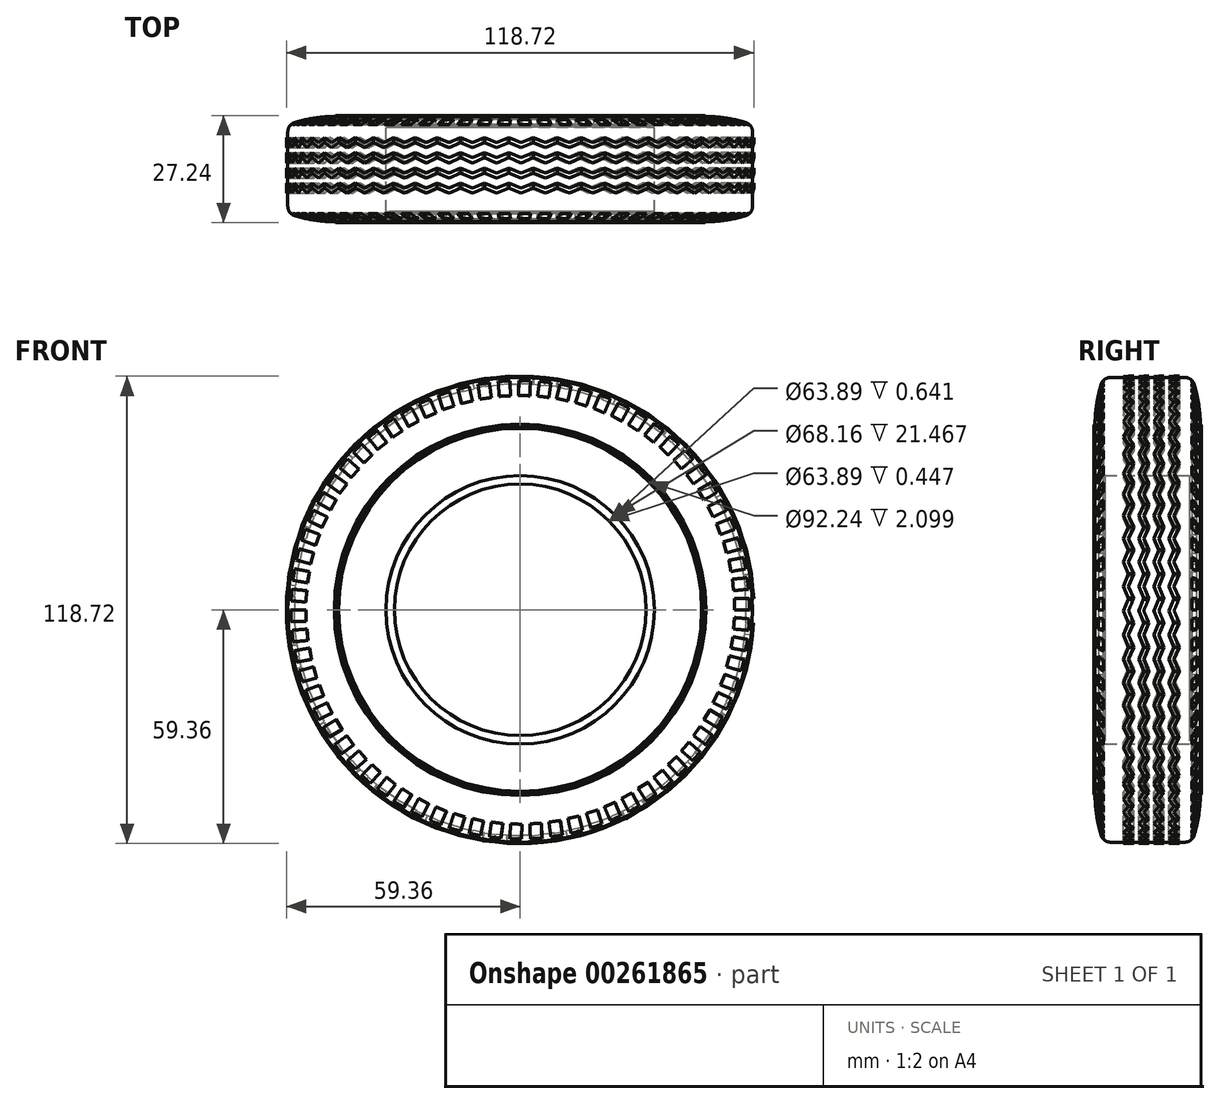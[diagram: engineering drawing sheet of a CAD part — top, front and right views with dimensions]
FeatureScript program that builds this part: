
annotation { "Feature Type Name" : "Feature", "Feature Type Description" : "" }
export const myFeature = defineFeature(function(context is Context, id is Id, definition is map)
    precondition{}
    {
        {
            var Q0;
            Q0=qCreatedBy(makeId("Front.planeOp"),FACE);
            var sketch = newSketch(context, id + "F0", { "sketchPlane" : qUnion([Q0])});
            skCircle(sketch, "E0", {"center": v(0, 0) * mm, "radius": 33.8 * mm});
            skSolve(sketch);
        }
        {
            var Q0;
            Q0=qCreatedBy(makeId("Top.planeOp"),FACE);
            var sketch = newSketch(context, id + "F1", { "sketchPlane" : qUnion([Q0])});
            skLineSegment(sketch, "E1", {"start": v(31.95, 0) * mm, "end": v(34.08, 0) * mm});
            skLineSegment(sketch, "E2", {"start": v(34.08, 22.56) * mm, "end": v(31.95, 22.56) * mm});
            skLineSegment(sketch, "E3", {"start": v(31.95, 22.56) * mm, "end": v(31.95, 21.91) * mm});
            skLineSegment(sketch, "E4", {"start": v(31.95, 21.91) * mm, "end": v(34.08, 21.91) * mm});
            skLineSegment(sketch, "E5", {"start": v(31.95, 0) * mm, "end": v(31.95, 0.45) * mm});
            skLineSegment(sketch, "E6", {"start": v(31.95, 0.45) * mm, "end": v(34.08, 0.45) * mm});
            skArc(sketch, "E7", {"start": v(59.04, 22.56) * mm, "mid": v(53.2, 24.07) * mm, "end": v(47.2, 24.65) * mm});
            skArc(sketch, "E8", {"start": v(34.08, 0) * mm, "mid": v(40.02, -1.54) * mm, "end": v(46.12, -2.1) * mm});
            skLineSegment(sketch, "E9", {"start": v(34.08, 21.91) * mm, "end": v(34.08, 0.45) * mm});
            skLineSegment(sketch, "E10", {"start": v(59.04, 22.56) * mm, "end": v(59.04, 0) * mm});
            skLineSegment(sketch, "E11", {"start": v(59.04, 22.56) * mm, "end": v(54.42, 22.56) * mm});
            skLineSegment(sketch, "E12", {"start": v(54.42, 22.56) * mm, "end": v(54.42, 23.84) * mm});
            skLineSegment(sketch, "E13", {"start": v(54.42, -1.28) * mm, "end": v(54.42, 0) * mm});
            skLineSegment(sketch, "E14", {"start": v(54.42, 0) * mm, "end": v(59.04, 0) * mm});
            skLineSegment(sketch, "E15", {"start": v(47.2, 24.65) * mm, "end": v(46.92, 24.9) * mm});
            skLineSegment(sketch, "E16", {"start": v(47.2, -2.1) * mm, "end": v(46.91, -2.34) * mm});
            skLineSegment(sketch, "E17", {"start": v(46.92, 24.9) * mm, "end": v(46.4, 24.9) * mm});
            skLineSegment(sketch, "E18", {"start": v(46.4, 24.9) * mm, "end": v(46.12, 24.65) * mm});
            skLineSegment(sketch, "E19", {"start": v(46.91, -2.34) * mm, "end": v(46.41, -2.34) * mm});
            skLineSegment(sketch, "E20", {"start": v(46.41, -2.34) * mm, "end": v(46.12, -2.1) * mm});
            skLineSegment(sketch, "E21", {"start": v(46.12, -2.1) * mm, "end": v(46.12, -2.1) * mm});
            skArc(sketch, "E22", {"start": v(47.2, -2.1) * mm, "mid": v(53.2, -1.52) * mm, "end": v(59.04, 0) * mm});
            skArc(sketch, "E23", {"start": v(46.12, 24.65) * mm, "mid": v(40.02, 24.1) * mm, "end": v(34.08, 22.56) * mm});
            skLineSegment(sketch, "E24", {"start": v(34.08, 0) * mm, "end": v(46.12, 0) * mm});
            skLineSegment(sketch, "E25", {"start": v(46.12, 0) * mm, "end": v(46.12, -2.1) * mm});
            skLineSegment(sketch, "E26", {"start": v(34.08, 22.56) * mm, "end": v(46.12, 22.56) * mm});
            skLineSegment(sketch, "E27", {"start": v(46.12, 22.56) * mm, "end": v(46.12, 24.65) * mm});
            skSolve(sketch);
        }
        {
            var Q0;
            Q0=makeQuery(id+"F1.imprint","IMPRINT",FACE,{"disambiguationData":[TD([[makeQuery(id+"F1.imprint","IMPRINT",EDGE,{"derivedFrom":sQuery(id+"F1.wireOp",EDGE,"E1")}),1.0]])]});
            var Q1;
            {var subQ0=sQuery(id+"F1.wireOp",EDGE,"E11");Q1=makeQuery(id+"F1.imprint","IMPRINT",FACE,{"disambiguationData":[TD([[makeQuery(id+"F1.imprint","IMPRINT",EDGE,{"derivedFrom":subQ0}),-1.0]])]});}
            var Q2;
            {var subQ2=sQuery(id+"F1.wireOp",EDGE,"E13");Q2=makeQuery(id+"F1.imprint","IMPRINT",FACE,{"disambiguationData":[TD([[makeQuery(id+"F1.imprint","IMPRINT",EDGE,{"derivedFrom":subQ2}),-1.0]])]});}
            var Q3;
            Q3=sQuery(id+"F0.wireOp",EDGE,"E0");
            revolve(context, id + "F2", {"entities" : qUnion([Q0, Q1, Q2]), "axis" : qUnion([Q3]), "revolveType" : RevolveType.FULL});
        }
        {
            var Q0;
            {var subQ0=sQuery(id+"F1.wireOp",EDGE,"E10");var subQ1=sQuery(id+"F1.wireOp",EDGE,"E14");Q0=makeQuery(id+"F6.opBoolean","SPLIT",EDGE,{"disambiguationData":[topologyDisambiguationEdgeConnected([makeQuery(id+"F2.opRevolve","SWEPT_FACE",FACE,{"disambiguationData":[OSD([subQ0])]}),makeQuery(id+"F5.opPattern","COPY",FACE,{"derivedFrom":makeQuery(id+"F4.opExtrude","SWEPT_FACE",FACE,{"disambiguationData":[OSD([subQ1])]}),"instanceName":"15"})])],"derivedFrom":makeQuery(id+"F2.opRevolve","SWEPT_EDGE",EDGE,{"disambiguationData":[OSD([subQ0,subQ1,sQuery(id+"F1.wireOp",EDGE,"E22")])]})});}
            var Q1;
            Q1=makeQuery(id+"F2.opRevolve","SWEPT_EDGE",EDGE,{"disambiguationData":[OSD([sQuery(id+"F1.wireOp",EDGE,"E7"),sQuery(id+"F1.wireOp",EDGE,"E10"),sQuery(id+"F1.wireOp",EDGE,"E11")])]});
            fillet(context, id + "F3", {"entities" : qUnion([Q0, Q1]), "radius" : 2.54 * mm, "tangentPropagation" : true, "allowEdgeOverflow" : false});
        }
        {
            var Q0;
            {var subQ0=sQuery(id+"F1.wireOp",EDGE,"E11");Q0=makeQuery(id+"F1.imprint","IMPRINT",FACE,{"disambiguationData":[TD([[makeQuery(id+"F1.imprint","IMPRINT",EDGE,{"derivedFrom":subQ0}),-1.0]])]});}
            var Q1;
            {var subQ2=sQuery(id+"F1.wireOp",EDGE,"E13");Q1=makeQuery(id+"F1.imprint","IMPRINT",FACE,{"disambiguationData":[TD([[makeQuery(id+"F1.imprint","IMPRINT",EDGE,{"derivedFrom":subQ2}),-1.0]])]});}
            extrude(context, id + "F4", {"entities" : qUnion([Q0, Q1]), "depth" : 2.92 * mm});
        }
        {
            var Q0;
            Q0=makeQuery(id+"F4.opExtrude","SWEPT_BODY",BODY,{"disambiguationData":[OSD([sQuery(id+"F1.wireOp",EDGE,"E7"),sQuery(id+"F1.wireOp",EDGE,"E11"),sQuery(id+"F1.wireOp",EDGE,"E12")])]});
            var Q1;
            Q1=makeQuery(id+"F4.opExtrude","SWEPT_BODY",BODY,{"disambiguationData":[OSD([sQuery(id+"F1.wireOp",EDGE,"E8"),sQuery(id+"F1.wireOp",EDGE,"E13"),sQuery(id+"F1.wireOp",EDGE,"E14")])]});
            var Q2;
            Q2=makeQuery(id+"F2.opRevolve","SWEPT_EDGE",EDGE,{"disambiguationData":[OSD([sQuery(id+"F1.wireOp",EDGE,"E1"),sQuery(id+"F1.wireOp",EDGE,"E5")])]});
            circularPattern(context, id + "F5", {"entities" : qUnion([Q0, Q1]), "axis" : qUnion([Q2]), "angle" : 360 * degree, "instanceCount" : 70, "equalSpace" : true});
        }
        {
            var Q0;
            Q0=makeQuery(id+"F4.opExtrude","SWEPT_BODY",BODY,{"disambiguationData":[OSD([sQuery(id+"F1.wireOp",EDGE,"E7"),sQuery(id+"F1.wireOp",EDGE,"E11"),sQuery(id+"F1.wireOp",EDGE,"E12")])]});
            var Q1;
            Q1=makeQuery(id+"F4.opExtrude","SWEPT_BODY",BODY,{"disambiguationData":[OSD([sQuery(id+"F1.wireOp",EDGE,"E8"),sQuery(id+"F1.wireOp",EDGE,"E13"),sQuery(id+"F1.wireOp",EDGE,"E14")])]});
            var Q2;
            Q2=makeQuery(id+"F5.opPattern","COPY",BODY,{"derivedFrom":makeQuery(id+"F4.opExtrude","SWEPT_BODY",BODY,{"disambiguationData":[OSD([sQuery(id+"F1.wireOp",EDGE,"E7"),sQuery(id+"F1.wireOp",EDGE,"E11"),sQuery(id+"F1.wireOp",EDGE,"E12")])]}),"instanceName":"1"});
            var Q3;
            Q3=makeQuery(id+"F5.opPattern","COPY",BODY,{"derivedFrom":makeQuery(id+"F4.opExtrude","SWEPT_BODY",BODY,{"disambiguationData":[OSD([sQuery(id+"F1.wireOp",EDGE,"E8"),sQuery(id+"F1.wireOp",EDGE,"E13"),sQuery(id+"F1.wireOp",EDGE,"E14")])]}),"instanceName":"1"});
            var Q4;
            Q4=makeQuery(id+"F5.opPattern","COPY",BODY,{"derivedFrom":makeQuery(id+"F4.opExtrude","SWEPT_BODY",BODY,{"disambiguationData":[OSD([sQuery(id+"F1.wireOp",EDGE,"E7"),sQuery(id+"F1.wireOp",EDGE,"E11"),sQuery(id+"F1.wireOp",EDGE,"E12")])]}),"instanceName":"2"});
            var Q5;
            Q5=makeQuery(id+"F5.opPattern","COPY",BODY,{"derivedFrom":makeQuery(id+"F4.opExtrude","SWEPT_BODY",BODY,{"disambiguationData":[OSD([sQuery(id+"F1.wireOp",EDGE,"E8"),sQuery(id+"F1.wireOp",EDGE,"E13"),sQuery(id+"F1.wireOp",EDGE,"E14")])]}),"instanceName":"2"});
            var Q6;
            Q6=makeQuery(id+"F5.opPattern","COPY",BODY,{"derivedFrom":makeQuery(id+"F4.opExtrude","SWEPT_BODY",BODY,{"disambiguationData":[OSD([sQuery(id+"F1.wireOp",EDGE,"E7"),sQuery(id+"F1.wireOp",EDGE,"E11"),sQuery(id+"F1.wireOp",EDGE,"E12")])]}),"instanceName":"3"});
            var Q7;
            Q7=makeQuery(id+"F5.opPattern","COPY",BODY,{"derivedFrom":makeQuery(id+"F4.opExtrude","SWEPT_BODY",BODY,{"disambiguationData":[OSD([sQuery(id+"F1.wireOp",EDGE,"E8"),sQuery(id+"F1.wireOp",EDGE,"E13"),sQuery(id+"F1.wireOp",EDGE,"E14")])]}),"instanceName":"3"});
            var Q8;
            Q8=makeQuery(id+"F5.opPattern","COPY",BODY,{"derivedFrom":makeQuery(id+"F4.opExtrude","SWEPT_BODY",BODY,{"disambiguationData":[OSD([sQuery(id+"F1.wireOp",EDGE,"E7"),sQuery(id+"F1.wireOp",EDGE,"E11"),sQuery(id+"F1.wireOp",EDGE,"E12")])]}),"instanceName":"4"});
            var Q9;
            Q9=makeQuery(id+"F5.opPattern","COPY",BODY,{"derivedFrom":makeQuery(id+"F4.opExtrude","SWEPT_BODY",BODY,{"disambiguationData":[OSD([sQuery(id+"F1.wireOp",EDGE,"E8"),sQuery(id+"F1.wireOp",EDGE,"E13"),sQuery(id+"F1.wireOp",EDGE,"E14")])]}),"instanceName":"4"});
            var Q10;
            Q10=makeQuery(id+"F5.opPattern","COPY",BODY,{"derivedFrom":makeQuery(id+"F4.opExtrude","SWEPT_BODY",BODY,{"disambiguationData":[OSD([sQuery(id+"F1.wireOp",EDGE,"E7"),sQuery(id+"F1.wireOp",EDGE,"E11"),sQuery(id+"F1.wireOp",EDGE,"E12")])]}),"instanceName":"5"});
            var Q11;
            Q11=makeQuery(id+"F5.opPattern","COPY",BODY,{"derivedFrom":makeQuery(id+"F4.opExtrude","SWEPT_BODY",BODY,{"disambiguationData":[OSD([sQuery(id+"F1.wireOp",EDGE,"E8"),sQuery(id+"F1.wireOp",EDGE,"E13"),sQuery(id+"F1.wireOp",EDGE,"E14")])]}),"instanceName":"5"});
            var Q12;
            Q12=makeQuery(id+"F5.opPattern","COPY",BODY,{"derivedFrom":makeQuery(id+"F4.opExtrude","SWEPT_BODY",BODY,{"disambiguationData":[OSD([sQuery(id+"F1.wireOp",EDGE,"E7"),sQuery(id+"F1.wireOp",EDGE,"E11"),sQuery(id+"F1.wireOp",EDGE,"E12")])]}),"instanceName":"6"});
            var Q13;
            Q13=makeQuery(id+"F5.opPattern","COPY",BODY,{"derivedFrom":makeQuery(id+"F4.opExtrude","SWEPT_BODY",BODY,{"disambiguationData":[OSD([sQuery(id+"F1.wireOp",EDGE,"E8"),sQuery(id+"F1.wireOp",EDGE,"E13"),sQuery(id+"F1.wireOp",EDGE,"E14")])]}),"instanceName":"6"});
            var Q14;
            Q14=makeQuery(id+"F5.opPattern","COPY",BODY,{"derivedFrom":makeQuery(id+"F4.opExtrude","SWEPT_BODY",BODY,{"disambiguationData":[OSD([sQuery(id+"F1.wireOp",EDGE,"E7"),sQuery(id+"F1.wireOp",EDGE,"E11"),sQuery(id+"F1.wireOp",EDGE,"E12")])]}),"instanceName":"7"});
            var Q15;
            Q15=makeQuery(id+"F5.opPattern","COPY",BODY,{"derivedFrom":makeQuery(id+"F4.opExtrude","SWEPT_BODY",BODY,{"disambiguationData":[OSD([sQuery(id+"F1.wireOp",EDGE,"E8"),sQuery(id+"F1.wireOp",EDGE,"E13"),sQuery(id+"F1.wireOp",EDGE,"E14")])]}),"instanceName":"7"});
            var Q16;
            Q16=makeQuery(id+"F5.opPattern","COPY",BODY,{"derivedFrom":makeQuery(id+"F4.opExtrude","SWEPT_BODY",BODY,{"disambiguationData":[OSD([sQuery(id+"F1.wireOp",EDGE,"E7"),sQuery(id+"F1.wireOp",EDGE,"E11"),sQuery(id+"F1.wireOp",EDGE,"E12")])]}),"instanceName":"8"});
            var Q17;
            Q17=makeQuery(id+"F5.opPattern","COPY",BODY,{"derivedFrom":makeQuery(id+"F4.opExtrude","SWEPT_BODY",BODY,{"disambiguationData":[OSD([sQuery(id+"F1.wireOp",EDGE,"E8"),sQuery(id+"F1.wireOp",EDGE,"E13"),sQuery(id+"F1.wireOp",EDGE,"E14")])]}),"instanceName":"8"});
            var Q18;
            Q18=makeQuery(id+"F5.opPattern","COPY",BODY,{"derivedFrom":makeQuery(id+"F4.opExtrude","SWEPT_BODY",BODY,{"disambiguationData":[OSD([sQuery(id+"F1.wireOp",EDGE,"E7"),sQuery(id+"F1.wireOp",EDGE,"E11"),sQuery(id+"F1.wireOp",EDGE,"E12")])]}),"instanceName":"9"});
            var Q19;
            Q19=makeQuery(id+"F5.opPattern","COPY",BODY,{"derivedFrom":makeQuery(id+"F4.opExtrude","SWEPT_BODY",BODY,{"disambiguationData":[OSD([sQuery(id+"F1.wireOp",EDGE,"E8"),sQuery(id+"F1.wireOp",EDGE,"E13"),sQuery(id+"F1.wireOp",EDGE,"E14")])]}),"instanceName":"9"});
            var Q20;
            Q20=makeQuery(id+"F5.opPattern","COPY",BODY,{"derivedFrom":makeQuery(id+"F4.opExtrude","SWEPT_BODY",BODY,{"disambiguationData":[OSD([sQuery(id+"F1.wireOp",EDGE,"E7"),sQuery(id+"F1.wireOp",EDGE,"E11"),sQuery(id+"F1.wireOp",EDGE,"E12")])]}),"instanceName":"10"});
            var Q21;
            Q21=makeQuery(id+"F5.opPattern","COPY",BODY,{"derivedFrom":makeQuery(id+"F4.opExtrude","SWEPT_BODY",BODY,{"disambiguationData":[OSD([sQuery(id+"F1.wireOp",EDGE,"E8"),sQuery(id+"F1.wireOp",EDGE,"E13"),sQuery(id+"F1.wireOp",EDGE,"E14")])]}),"instanceName":"10"});
            var Q22;
            Q22=makeQuery(id+"F5.opPattern","COPY",BODY,{"derivedFrom":makeQuery(id+"F4.opExtrude","SWEPT_BODY",BODY,{"disambiguationData":[OSD([sQuery(id+"F1.wireOp",EDGE,"E7"),sQuery(id+"F1.wireOp",EDGE,"E11"),sQuery(id+"F1.wireOp",EDGE,"E12")])]}),"instanceName":"11"});
            var Q23;
            Q23=makeQuery(id+"F5.opPattern","COPY",BODY,{"derivedFrom":makeQuery(id+"F4.opExtrude","SWEPT_BODY",BODY,{"disambiguationData":[OSD([sQuery(id+"F1.wireOp",EDGE,"E8"),sQuery(id+"F1.wireOp",EDGE,"E13"),sQuery(id+"F1.wireOp",EDGE,"E14")])]}),"instanceName":"11"});
            var Q24;
            Q24=makeQuery(id+"F5.opPattern","COPY",BODY,{"derivedFrom":makeQuery(id+"F4.opExtrude","SWEPT_BODY",BODY,{"disambiguationData":[OSD([sQuery(id+"F1.wireOp",EDGE,"E7"),sQuery(id+"F1.wireOp",EDGE,"E11"),sQuery(id+"F1.wireOp",EDGE,"E12")])]}),"instanceName":"12"});
            var Q25;
            Q25=makeQuery(id+"F5.opPattern","COPY",BODY,{"derivedFrom":makeQuery(id+"F4.opExtrude","SWEPT_BODY",BODY,{"disambiguationData":[OSD([sQuery(id+"F1.wireOp",EDGE,"E8"),sQuery(id+"F1.wireOp",EDGE,"E13"),sQuery(id+"F1.wireOp",EDGE,"E14")])]}),"instanceName":"12"});
            var Q26;
            Q26=makeQuery(id+"F5.opPattern","COPY",BODY,{"derivedFrom":makeQuery(id+"F4.opExtrude","SWEPT_BODY",BODY,{"disambiguationData":[OSD([sQuery(id+"F1.wireOp",EDGE,"E7"),sQuery(id+"F1.wireOp",EDGE,"E11"),sQuery(id+"F1.wireOp",EDGE,"E12")])]}),"instanceName":"13"});
            var Q27;
            Q27=makeQuery(id+"F5.opPattern","COPY",BODY,{"derivedFrom":makeQuery(id+"F4.opExtrude","SWEPT_BODY",BODY,{"disambiguationData":[OSD([sQuery(id+"F1.wireOp",EDGE,"E8"),sQuery(id+"F1.wireOp",EDGE,"E13"),sQuery(id+"F1.wireOp",EDGE,"E14")])]}),"instanceName":"13"});
            var Q28;
            Q28=makeQuery(id+"F5.opPattern","COPY",BODY,{"derivedFrom":makeQuery(id+"F4.opExtrude","SWEPT_BODY",BODY,{"disambiguationData":[OSD([sQuery(id+"F1.wireOp",EDGE,"E7"),sQuery(id+"F1.wireOp",EDGE,"E11"),sQuery(id+"F1.wireOp",EDGE,"E12")])]}),"instanceName":"14"});
            var Q29;
            Q29=makeQuery(id+"F5.opPattern","COPY",BODY,{"derivedFrom":makeQuery(id+"F4.opExtrude","SWEPT_BODY",BODY,{"disambiguationData":[OSD([sQuery(id+"F1.wireOp",EDGE,"E8"),sQuery(id+"F1.wireOp",EDGE,"E13"),sQuery(id+"F1.wireOp",EDGE,"E14")])]}),"instanceName":"14"});
            var Q30;
            Q30=makeQuery(id+"F5.opPattern","COPY",BODY,{"derivedFrom":makeQuery(id+"F4.opExtrude","SWEPT_BODY",BODY,{"disambiguationData":[OSD([sQuery(id+"F1.wireOp",EDGE,"E7"),sQuery(id+"F1.wireOp",EDGE,"E11"),sQuery(id+"F1.wireOp",EDGE,"E12")])]}),"instanceName":"15"});
            var Q31;
            Q31=makeQuery(id+"F5.opPattern","COPY",BODY,{"derivedFrom":makeQuery(id+"F4.opExtrude","SWEPT_BODY",BODY,{"disambiguationData":[OSD([sQuery(id+"F1.wireOp",EDGE,"E8"),sQuery(id+"F1.wireOp",EDGE,"E13"),sQuery(id+"F1.wireOp",EDGE,"E14")])]}),"instanceName":"15"});
            var Q32;
            Q32=makeQuery(id+"F5.opPattern","COPY",BODY,{"derivedFrom":makeQuery(id+"F4.opExtrude","SWEPT_BODY",BODY,{"disambiguationData":[OSD([sQuery(id+"F1.wireOp",EDGE,"E7"),sQuery(id+"F1.wireOp",EDGE,"E11"),sQuery(id+"F1.wireOp",EDGE,"E12")])]}),"instanceName":"16"});
            var Q33;
            Q33=makeQuery(id+"F5.opPattern","COPY",BODY,{"derivedFrom":makeQuery(id+"F4.opExtrude","SWEPT_BODY",BODY,{"disambiguationData":[OSD([sQuery(id+"F1.wireOp",EDGE,"E8"),sQuery(id+"F1.wireOp",EDGE,"E13"),sQuery(id+"F1.wireOp",EDGE,"E14")])]}),"instanceName":"16"});
            var Q34;
            Q34=makeQuery(id+"F5.opPattern","COPY",BODY,{"derivedFrom":makeQuery(id+"F4.opExtrude","SWEPT_BODY",BODY,{"disambiguationData":[OSD([sQuery(id+"F1.wireOp",EDGE,"E7"),sQuery(id+"F1.wireOp",EDGE,"E11"),sQuery(id+"F1.wireOp",EDGE,"E12")])]}),"instanceName":"17"});
            var Q35;
            Q35=makeQuery(id+"F5.opPattern","COPY",BODY,{"derivedFrom":makeQuery(id+"F4.opExtrude","SWEPT_BODY",BODY,{"disambiguationData":[OSD([sQuery(id+"F1.wireOp",EDGE,"E8"),sQuery(id+"F1.wireOp",EDGE,"E13"),sQuery(id+"F1.wireOp",EDGE,"E14")])]}),"instanceName":"17"});
            var Q36;
            Q36=makeQuery(id+"F5.opPattern","COPY",BODY,{"derivedFrom":makeQuery(id+"F4.opExtrude","SWEPT_BODY",BODY,{"disambiguationData":[OSD([sQuery(id+"F1.wireOp",EDGE,"E7"),sQuery(id+"F1.wireOp",EDGE,"E11"),sQuery(id+"F1.wireOp",EDGE,"E12")])]}),"instanceName":"18"});
            var Q37;
            Q37=makeQuery(id+"F5.opPattern","COPY",BODY,{"derivedFrom":makeQuery(id+"F4.opExtrude","SWEPT_BODY",BODY,{"disambiguationData":[OSD([sQuery(id+"F1.wireOp",EDGE,"E8"),sQuery(id+"F1.wireOp",EDGE,"E13"),sQuery(id+"F1.wireOp",EDGE,"E14")])]}),"instanceName":"18"});
            var Q38;
            Q38=makeQuery(id+"F5.opPattern","COPY",BODY,{"derivedFrom":makeQuery(id+"F4.opExtrude","SWEPT_BODY",BODY,{"disambiguationData":[OSD([sQuery(id+"F1.wireOp",EDGE,"E7"),sQuery(id+"F1.wireOp",EDGE,"E11"),sQuery(id+"F1.wireOp",EDGE,"E12")])]}),"instanceName":"19"});
            var Q39;
            Q39=makeQuery(id+"F5.opPattern","COPY",BODY,{"derivedFrom":makeQuery(id+"F4.opExtrude","SWEPT_BODY",BODY,{"disambiguationData":[OSD([sQuery(id+"F1.wireOp",EDGE,"E8"),sQuery(id+"F1.wireOp",EDGE,"E13"),sQuery(id+"F1.wireOp",EDGE,"E14")])]}),"instanceName":"19"});
            var Q40;
            Q40=makeQuery(id+"F5.opPattern","COPY",BODY,{"derivedFrom":makeQuery(id+"F4.opExtrude","SWEPT_BODY",BODY,{"disambiguationData":[OSD([sQuery(id+"F1.wireOp",EDGE,"E7"),sQuery(id+"F1.wireOp",EDGE,"E11"),sQuery(id+"F1.wireOp",EDGE,"E12")])]}),"instanceName":"20"});
            var Q41;
            Q41=makeQuery(id+"F5.opPattern","COPY",BODY,{"derivedFrom":makeQuery(id+"F4.opExtrude","SWEPT_BODY",BODY,{"disambiguationData":[OSD([sQuery(id+"F1.wireOp",EDGE,"E8"),sQuery(id+"F1.wireOp",EDGE,"E13"),sQuery(id+"F1.wireOp",EDGE,"E14")])]}),"instanceName":"20"});
            var Q42;
            Q42=makeQuery(id+"F5.opPattern","COPY",BODY,{"derivedFrom":makeQuery(id+"F4.opExtrude","SWEPT_BODY",BODY,{"disambiguationData":[OSD([sQuery(id+"F1.wireOp",EDGE,"E7"),sQuery(id+"F1.wireOp",EDGE,"E11"),sQuery(id+"F1.wireOp",EDGE,"E12")])]}),"instanceName":"21"});
            var Q43;
            Q43=makeQuery(id+"F5.opPattern","COPY",BODY,{"derivedFrom":makeQuery(id+"F4.opExtrude","SWEPT_BODY",BODY,{"disambiguationData":[OSD([sQuery(id+"F1.wireOp",EDGE,"E8"),sQuery(id+"F1.wireOp",EDGE,"E13"),sQuery(id+"F1.wireOp",EDGE,"E14")])]}),"instanceName":"21"});
            var Q44;
            Q44=makeQuery(id+"F5.opPattern","COPY",BODY,{"derivedFrom":makeQuery(id+"F4.opExtrude","SWEPT_BODY",BODY,{"disambiguationData":[OSD([sQuery(id+"F1.wireOp",EDGE,"E7"),sQuery(id+"F1.wireOp",EDGE,"E11"),sQuery(id+"F1.wireOp",EDGE,"E12")])]}),"instanceName":"22"});
            var Q45;
            Q45=makeQuery(id+"F5.opPattern","COPY",BODY,{"derivedFrom":makeQuery(id+"F4.opExtrude","SWEPT_BODY",BODY,{"disambiguationData":[OSD([sQuery(id+"F1.wireOp",EDGE,"E8"),sQuery(id+"F1.wireOp",EDGE,"E13"),sQuery(id+"F1.wireOp",EDGE,"E14")])]}),"instanceName":"22"});
            var Q46;
            Q46=makeQuery(id+"F5.opPattern","COPY",BODY,{"derivedFrom":makeQuery(id+"F4.opExtrude","SWEPT_BODY",BODY,{"disambiguationData":[OSD([sQuery(id+"F1.wireOp",EDGE,"E7"),sQuery(id+"F1.wireOp",EDGE,"E11"),sQuery(id+"F1.wireOp",EDGE,"E12")])]}),"instanceName":"23"});
            var Q47;
            Q47=makeQuery(id+"F5.opPattern","COPY",BODY,{"derivedFrom":makeQuery(id+"F4.opExtrude","SWEPT_BODY",BODY,{"disambiguationData":[OSD([sQuery(id+"F1.wireOp",EDGE,"E8"),sQuery(id+"F1.wireOp",EDGE,"E13"),sQuery(id+"F1.wireOp",EDGE,"E14")])]}),"instanceName":"23"});
            var Q48;
            Q48=makeQuery(id+"F5.opPattern","COPY",BODY,{"derivedFrom":makeQuery(id+"F4.opExtrude","SWEPT_BODY",BODY,{"disambiguationData":[OSD([sQuery(id+"F1.wireOp",EDGE,"E7"),sQuery(id+"F1.wireOp",EDGE,"E11"),sQuery(id+"F1.wireOp",EDGE,"E12")])]}),"instanceName":"24"});
            var Q49;
            Q49=makeQuery(id+"F5.opPattern","COPY",BODY,{"derivedFrom":makeQuery(id+"F4.opExtrude","SWEPT_BODY",BODY,{"disambiguationData":[OSD([sQuery(id+"F1.wireOp",EDGE,"E8"),sQuery(id+"F1.wireOp",EDGE,"E13"),sQuery(id+"F1.wireOp",EDGE,"E14")])]}),"instanceName":"24"});
            var Q50;
            Q50=makeQuery(id+"F5.opPattern","COPY",BODY,{"derivedFrom":makeQuery(id+"F4.opExtrude","SWEPT_BODY",BODY,{"disambiguationData":[OSD([sQuery(id+"F1.wireOp",EDGE,"E7"),sQuery(id+"F1.wireOp",EDGE,"E11"),sQuery(id+"F1.wireOp",EDGE,"E12")])]}),"instanceName":"25"});
            var Q51;
            Q51=makeQuery(id+"F5.opPattern","COPY",BODY,{"derivedFrom":makeQuery(id+"F4.opExtrude","SWEPT_BODY",BODY,{"disambiguationData":[OSD([sQuery(id+"F1.wireOp",EDGE,"E8"),sQuery(id+"F1.wireOp",EDGE,"E13"),sQuery(id+"F1.wireOp",EDGE,"E14")])]}),"instanceName":"25"});
            var Q52;
            Q52=makeQuery(id+"F5.opPattern","COPY",BODY,{"derivedFrom":makeQuery(id+"F4.opExtrude","SWEPT_BODY",BODY,{"disambiguationData":[OSD([sQuery(id+"F1.wireOp",EDGE,"E7"),sQuery(id+"F1.wireOp",EDGE,"E11"),sQuery(id+"F1.wireOp",EDGE,"E12")])]}),"instanceName":"26"});
            var Q53;
            Q53=makeQuery(id+"F5.opPattern","COPY",BODY,{"derivedFrom":makeQuery(id+"F4.opExtrude","SWEPT_BODY",BODY,{"disambiguationData":[OSD([sQuery(id+"F1.wireOp",EDGE,"E8"),sQuery(id+"F1.wireOp",EDGE,"E13"),sQuery(id+"F1.wireOp",EDGE,"E14")])]}),"instanceName":"26"});
            var Q54;
            Q54=makeQuery(id+"F5.opPattern","COPY",BODY,{"derivedFrom":makeQuery(id+"F4.opExtrude","SWEPT_BODY",BODY,{"disambiguationData":[OSD([sQuery(id+"F1.wireOp",EDGE,"E7"),sQuery(id+"F1.wireOp",EDGE,"E11"),sQuery(id+"F1.wireOp",EDGE,"E12")])]}),"instanceName":"27"});
            var Q55;
            Q55=makeQuery(id+"F5.opPattern","COPY",BODY,{"derivedFrom":makeQuery(id+"F4.opExtrude","SWEPT_BODY",BODY,{"disambiguationData":[OSD([sQuery(id+"F1.wireOp",EDGE,"E8"),sQuery(id+"F1.wireOp",EDGE,"E13"),sQuery(id+"F1.wireOp",EDGE,"E14")])]}),"instanceName":"27"});
            var Q56;
            Q56=makeQuery(id+"F5.opPattern","COPY",BODY,{"derivedFrom":makeQuery(id+"F4.opExtrude","SWEPT_BODY",BODY,{"disambiguationData":[OSD([sQuery(id+"F1.wireOp",EDGE,"E7"),sQuery(id+"F1.wireOp",EDGE,"E11"),sQuery(id+"F1.wireOp",EDGE,"E12")])]}),"instanceName":"28"});
            var Q57;
            Q57=makeQuery(id+"F5.opPattern","COPY",BODY,{"derivedFrom":makeQuery(id+"F4.opExtrude","SWEPT_BODY",BODY,{"disambiguationData":[OSD([sQuery(id+"F1.wireOp",EDGE,"E8"),sQuery(id+"F1.wireOp",EDGE,"E13"),sQuery(id+"F1.wireOp",EDGE,"E14")])]}),"instanceName":"28"});
            var Q58;
            Q58=makeQuery(id+"F5.opPattern","COPY",BODY,{"derivedFrom":makeQuery(id+"F4.opExtrude","SWEPT_BODY",BODY,{"disambiguationData":[OSD([sQuery(id+"F1.wireOp",EDGE,"E7"),sQuery(id+"F1.wireOp",EDGE,"E11"),sQuery(id+"F1.wireOp",EDGE,"E12")])]}),"instanceName":"29"});
            var Q59;
            Q59=makeQuery(id+"F5.opPattern","COPY",BODY,{"derivedFrom":makeQuery(id+"F4.opExtrude","SWEPT_BODY",BODY,{"disambiguationData":[OSD([sQuery(id+"F1.wireOp",EDGE,"E8"),sQuery(id+"F1.wireOp",EDGE,"E13"),sQuery(id+"F1.wireOp",EDGE,"E14")])]}),"instanceName":"29"});
            var Q60;
            Q60=makeQuery(id+"F5.opPattern","COPY",BODY,{"derivedFrom":makeQuery(id+"F4.opExtrude","SWEPT_BODY",BODY,{"disambiguationData":[OSD([sQuery(id+"F1.wireOp",EDGE,"E7"),sQuery(id+"F1.wireOp",EDGE,"E11"),sQuery(id+"F1.wireOp",EDGE,"E12")])]}),"instanceName":"30"});
            var Q61;
            Q61=makeQuery(id+"F5.opPattern","COPY",BODY,{"derivedFrom":makeQuery(id+"F4.opExtrude","SWEPT_BODY",BODY,{"disambiguationData":[OSD([sQuery(id+"F1.wireOp",EDGE,"E8"),sQuery(id+"F1.wireOp",EDGE,"E13"),sQuery(id+"F1.wireOp",EDGE,"E14")])]}),"instanceName":"30"});
            var Q62;
            Q62=makeQuery(id+"F5.opPattern","COPY",BODY,{"derivedFrom":makeQuery(id+"F4.opExtrude","SWEPT_BODY",BODY,{"disambiguationData":[OSD([sQuery(id+"F1.wireOp",EDGE,"E7"),sQuery(id+"F1.wireOp",EDGE,"E11"),sQuery(id+"F1.wireOp",EDGE,"E12")])]}),"instanceName":"31"});
            var Q63;
            Q63=makeQuery(id+"F5.opPattern","COPY",BODY,{"derivedFrom":makeQuery(id+"F4.opExtrude","SWEPT_BODY",BODY,{"disambiguationData":[OSD([sQuery(id+"F1.wireOp",EDGE,"E8"),sQuery(id+"F1.wireOp",EDGE,"E13"),sQuery(id+"F1.wireOp",EDGE,"E14")])]}),"instanceName":"31"});
            var Q64;
            Q64=makeQuery(id+"F5.opPattern","COPY",BODY,{"derivedFrom":makeQuery(id+"F4.opExtrude","SWEPT_BODY",BODY,{"disambiguationData":[OSD([sQuery(id+"F1.wireOp",EDGE,"E7"),sQuery(id+"F1.wireOp",EDGE,"E11"),sQuery(id+"F1.wireOp",EDGE,"E12")])]}),"instanceName":"32"});
            var Q65;
            Q65=makeQuery(id+"F5.opPattern","COPY",BODY,{"derivedFrom":makeQuery(id+"F4.opExtrude","SWEPT_BODY",BODY,{"disambiguationData":[OSD([sQuery(id+"F1.wireOp",EDGE,"E8"),sQuery(id+"F1.wireOp",EDGE,"E13"),sQuery(id+"F1.wireOp",EDGE,"E14")])]}),"instanceName":"32"});
            var Q66;
            Q66=makeQuery(id+"F5.opPattern","COPY",BODY,{"derivedFrom":makeQuery(id+"F4.opExtrude","SWEPT_BODY",BODY,{"disambiguationData":[OSD([sQuery(id+"F1.wireOp",EDGE,"E7"),sQuery(id+"F1.wireOp",EDGE,"E11"),sQuery(id+"F1.wireOp",EDGE,"E12")])]}),"instanceName":"33"});
            var Q67;
            Q67=makeQuery(id+"F5.opPattern","COPY",BODY,{"derivedFrom":makeQuery(id+"F4.opExtrude","SWEPT_BODY",BODY,{"disambiguationData":[OSD([sQuery(id+"F1.wireOp",EDGE,"E8"),sQuery(id+"F1.wireOp",EDGE,"E13"),sQuery(id+"F1.wireOp",EDGE,"E14")])]}),"instanceName":"33"});
            var Q68;
            Q68=makeQuery(id+"F5.opPattern","COPY",BODY,{"derivedFrom":makeQuery(id+"F4.opExtrude","SWEPT_BODY",BODY,{"disambiguationData":[OSD([sQuery(id+"F1.wireOp",EDGE,"E7"),sQuery(id+"F1.wireOp",EDGE,"E11"),sQuery(id+"F1.wireOp",EDGE,"E12")])]}),"instanceName":"34"});
            var Q69;
            Q69=makeQuery(id+"F5.opPattern","COPY",BODY,{"derivedFrom":makeQuery(id+"F4.opExtrude","SWEPT_BODY",BODY,{"disambiguationData":[OSD([sQuery(id+"F1.wireOp",EDGE,"E8"),sQuery(id+"F1.wireOp",EDGE,"E13"),sQuery(id+"F1.wireOp",EDGE,"E14")])]}),"instanceName":"34"});
            var Q70;
            Q70=makeQuery(id+"F5.opPattern","COPY",BODY,{"derivedFrom":makeQuery(id+"F4.opExtrude","SWEPT_BODY",BODY,{"disambiguationData":[OSD([sQuery(id+"F1.wireOp",EDGE,"E7"),sQuery(id+"F1.wireOp",EDGE,"E11"),sQuery(id+"F1.wireOp",EDGE,"E12")])]}),"instanceName":"35"});
            var Q71;
            Q71=makeQuery(id+"F5.opPattern","COPY",BODY,{"derivedFrom":makeQuery(id+"F4.opExtrude","SWEPT_BODY",BODY,{"disambiguationData":[OSD([sQuery(id+"F1.wireOp",EDGE,"E8"),sQuery(id+"F1.wireOp",EDGE,"E13"),sQuery(id+"F1.wireOp",EDGE,"E14")])]}),"instanceName":"35"});
            var Q72;
            Q72=makeQuery(id+"F5.opPattern","COPY",BODY,{"derivedFrom":makeQuery(id+"F4.opExtrude","SWEPT_BODY",BODY,{"disambiguationData":[OSD([sQuery(id+"F1.wireOp",EDGE,"E7"),sQuery(id+"F1.wireOp",EDGE,"E11"),sQuery(id+"F1.wireOp",EDGE,"E12")])]}),"instanceName":"36"});
            var Q73;
            Q73=makeQuery(id+"F5.opPattern","COPY",BODY,{"derivedFrom":makeQuery(id+"F4.opExtrude","SWEPT_BODY",BODY,{"disambiguationData":[OSD([sQuery(id+"F1.wireOp",EDGE,"E8"),sQuery(id+"F1.wireOp",EDGE,"E13"),sQuery(id+"F1.wireOp",EDGE,"E14")])]}),"instanceName":"36"});
            var Q74;
            Q74=makeQuery(id+"F5.opPattern","COPY",BODY,{"derivedFrom":makeQuery(id+"F4.opExtrude","SWEPT_BODY",BODY,{"disambiguationData":[OSD([sQuery(id+"F1.wireOp",EDGE,"E7"),sQuery(id+"F1.wireOp",EDGE,"E11"),sQuery(id+"F1.wireOp",EDGE,"E12")])]}),"instanceName":"37"});
            var Q75;
            Q75=makeQuery(id+"F5.opPattern","COPY",BODY,{"derivedFrom":makeQuery(id+"F4.opExtrude","SWEPT_BODY",BODY,{"disambiguationData":[OSD([sQuery(id+"F1.wireOp",EDGE,"E8"),sQuery(id+"F1.wireOp",EDGE,"E13"),sQuery(id+"F1.wireOp",EDGE,"E14")])]}),"instanceName":"37"});
            var Q76;
            Q76=makeQuery(id+"F5.opPattern","COPY",BODY,{"derivedFrom":makeQuery(id+"F4.opExtrude","SWEPT_BODY",BODY,{"disambiguationData":[OSD([sQuery(id+"F1.wireOp",EDGE,"E7"),sQuery(id+"F1.wireOp",EDGE,"E11"),sQuery(id+"F1.wireOp",EDGE,"E12")])]}),"instanceName":"38"});
            var Q77;
            Q77=makeQuery(id+"F5.opPattern","COPY",BODY,{"derivedFrom":makeQuery(id+"F4.opExtrude","SWEPT_BODY",BODY,{"disambiguationData":[OSD([sQuery(id+"F1.wireOp",EDGE,"E8"),sQuery(id+"F1.wireOp",EDGE,"E13"),sQuery(id+"F1.wireOp",EDGE,"E14")])]}),"instanceName":"38"});
            var Q78;
            Q78=makeQuery(id+"F5.opPattern","COPY",BODY,{"derivedFrom":makeQuery(id+"F4.opExtrude","SWEPT_BODY",BODY,{"disambiguationData":[OSD([sQuery(id+"F1.wireOp",EDGE,"E7"),sQuery(id+"F1.wireOp",EDGE,"E11"),sQuery(id+"F1.wireOp",EDGE,"E12")])]}),"instanceName":"39"});
            var Q79;
            Q79=makeQuery(id+"F5.opPattern","COPY",BODY,{"derivedFrom":makeQuery(id+"F4.opExtrude","SWEPT_BODY",BODY,{"disambiguationData":[OSD([sQuery(id+"F1.wireOp",EDGE,"E8"),sQuery(id+"F1.wireOp",EDGE,"E13"),sQuery(id+"F1.wireOp",EDGE,"E14")])]}),"instanceName":"39"});
            var Q80;
            Q80=makeQuery(id+"F5.opPattern","COPY",BODY,{"derivedFrom":makeQuery(id+"F4.opExtrude","SWEPT_BODY",BODY,{"disambiguationData":[OSD([sQuery(id+"F1.wireOp",EDGE,"E7"),sQuery(id+"F1.wireOp",EDGE,"E11"),sQuery(id+"F1.wireOp",EDGE,"E12")])]}),"instanceName":"40"});
            var Q81;
            Q81=makeQuery(id+"F5.opPattern","COPY",BODY,{"derivedFrom":makeQuery(id+"F4.opExtrude","SWEPT_BODY",BODY,{"disambiguationData":[OSD([sQuery(id+"F1.wireOp",EDGE,"E8"),sQuery(id+"F1.wireOp",EDGE,"E13"),sQuery(id+"F1.wireOp",EDGE,"E14")])]}),"instanceName":"40"});
            var Q82;
            Q82=makeQuery(id+"F5.opPattern","COPY",BODY,{"derivedFrom":makeQuery(id+"F4.opExtrude","SWEPT_BODY",BODY,{"disambiguationData":[OSD([sQuery(id+"F1.wireOp",EDGE,"E7"),sQuery(id+"F1.wireOp",EDGE,"E11"),sQuery(id+"F1.wireOp",EDGE,"E12")])]}),"instanceName":"41"});
            var Q83;
            Q83=makeQuery(id+"F5.opPattern","COPY",BODY,{"derivedFrom":makeQuery(id+"F4.opExtrude","SWEPT_BODY",BODY,{"disambiguationData":[OSD([sQuery(id+"F1.wireOp",EDGE,"E8"),sQuery(id+"F1.wireOp",EDGE,"E13"),sQuery(id+"F1.wireOp",EDGE,"E14")])]}),"instanceName":"41"});
            var Q84;
            Q84=makeQuery(id+"F5.opPattern","COPY",BODY,{"derivedFrom":makeQuery(id+"F4.opExtrude","SWEPT_BODY",BODY,{"disambiguationData":[OSD([sQuery(id+"F1.wireOp",EDGE,"E7"),sQuery(id+"F1.wireOp",EDGE,"E11"),sQuery(id+"F1.wireOp",EDGE,"E12")])]}),"instanceName":"42"});
            var Q85;
            Q85=makeQuery(id+"F5.opPattern","COPY",BODY,{"derivedFrom":makeQuery(id+"F4.opExtrude","SWEPT_BODY",BODY,{"disambiguationData":[OSD([sQuery(id+"F1.wireOp",EDGE,"E8"),sQuery(id+"F1.wireOp",EDGE,"E13"),sQuery(id+"F1.wireOp",EDGE,"E14")])]}),"instanceName":"42"});
            var Q86;
            Q86=makeQuery(id+"F5.opPattern","COPY",BODY,{"derivedFrom":makeQuery(id+"F4.opExtrude","SWEPT_BODY",BODY,{"disambiguationData":[OSD([sQuery(id+"F1.wireOp",EDGE,"E7"),sQuery(id+"F1.wireOp",EDGE,"E11"),sQuery(id+"F1.wireOp",EDGE,"E12")])]}),"instanceName":"43"});
            var Q87;
            Q87=makeQuery(id+"F5.opPattern","COPY",BODY,{"derivedFrom":makeQuery(id+"F4.opExtrude","SWEPT_BODY",BODY,{"disambiguationData":[OSD([sQuery(id+"F1.wireOp",EDGE,"E8"),sQuery(id+"F1.wireOp",EDGE,"E13"),sQuery(id+"F1.wireOp",EDGE,"E14")])]}),"instanceName":"43"});
            var Q88;
            Q88=makeQuery(id+"F5.opPattern","COPY",BODY,{"derivedFrom":makeQuery(id+"F4.opExtrude","SWEPT_BODY",BODY,{"disambiguationData":[OSD([sQuery(id+"F1.wireOp",EDGE,"E7"),sQuery(id+"F1.wireOp",EDGE,"E11"),sQuery(id+"F1.wireOp",EDGE,"E12")])]}),"instanceName":"44"});
            var Q89;
            Q89=makeQuery(id+"F5.opPattern","COPY",BODY,{"derivedFrom":makeQuery(id+"F4.opExtrude","SWEPT_BODY",BODY,{"disambiguationData":[OSD([sQuery(id+"F1.wireOp",EDGE,"E8"),sQuery(id+"F1.wireOp",EDGE,"E13"),sQuery(id+"F1.wireOp",EDGE,"E14")])]}),"instanceName":"44"});
            var Q90;
            Q90=makeQuery(id+"F5.opPattern","COPY",BODY,{"derivedFrom":makeQuery(id+"F4.opExtrude","SWEPT_BODY",BODY,{"disambiguationData":[OSD([sQuery(id+"F1.wireOp",EDGE,"E7"),sQuery(id+"F1.wireOp",EDGE,"E11"),sQuery(id+"F1.wireOp",EDGE,"E12")])]}),"instanceName":"45"});
            var Q91;
            Q91=makeQuery(id+"F5.opPattern","COPY",BODY,{"derivedFrom":makeQuery(id+"F4.opExtrude","SWEPT_BODY",BODY,{"disambiguationData":[OSD([sQuery(id+"F1.wireOp",EDGE,"E8"),sQuery(id+"F1.wireOp",EDGE,"E13"),sQuery(id+"F1.wireOp",EDGE,"E14")])]}),"instanceName":"45"});
            var Q92;
            Q92=makeQuery(id+"F5.opPattern","COPY",BODY,{"derivedFrom":makeQuery(id+"F4.opExtrude","SWEPT_BODY",BODY,{"disambiguationData":[OSD([sQuery(id+"F1.wireOp",EDGE,"E7"),sQuery(id+"F1.wireOp",EDGE,"E11"),sQuery(id+"F1.wireOp",EDGE,"E12")])]}),"instanceName":"46"});
            var Q93;
            Q93=makeQuery(id+"F5.opPattern","COPY",BODY,{"derivedFrom":makeQuery(id+"F4.opExtrude","SWEPT_BODY",BODY,{"disambiguationData":[OSD([sQuery(id+"F1.wireOp",EDGE,"E8"),sQuery(id+"F1.wireOp",EDGE,"E13"),sQuery(id+"F1.wireOp",EDGE,"E14")])]}),"instanceName":"46"});
            var Q94;
            Q94=makeQuery(id+"F5.opPattern","COPY",BODY,{"derivedFrom":makeQuery(id+"F4.opExtrude","SWEPT_BODY",BODY,{"disambiguationData":[OSD([sQuery(id+"F1.wireOp",EDGE,"E7"),sQuery(id+"F1.wireOp",EDGE,"E11"),sQuery(id+"F1.wireOp",EDGE,"E12")])]}),"instanceName":"47"});
            var Q95;
            Q95=makeQuery(id+"F5.opPattern","COPY",BODY,{"derivedFrom":makeQuery(id+"F4.opExtrude","SWEPT_BODY",BODY,{"disambiguationData":[OSD([sQuery(id+"F1.wireOp",EDGE,"E8"),sQuery(id+"F1.wireOp",EDGE,"E13"),sQuery(id+"F1.wireOp",EDGE,"E14")])]}),"instanceName":"47"});
            var Q96;
            Q96=makeQuery(id+"F5.opPattern","COPY",BODY,{"derivedFrom":makeQuery(id+"F4.opExtrude","SWEPT_BODY",BODY,{"disambiguationData":[OSD([sQuery(id+"F1.wireOp",EDGE,"E7"),sQuery(id+"F1.wireOp",EDGE,"E11"),sQuery(id+"F1.wireOp",EDGE,"E12")])]}),"instanceName":"48"});
            var Q97;
            Q97=makeQuery(id+"F5.opPattern","COPY",BODY,{"derivedFrom":makeQuery(id+"F4.opExtrude","SWEPT_BODY",BODY,{"disambiguationData":[OSD([sQuery(id+"F1.wireOp",EDGE,"E8"),sQuery(id+"F1.wireOp",EDGE,"E13"),sQuery(id+"F1.wireOp",EDGE,"E14")])]}),"instanceName":"48"});
            var Q98;
            Q98=makeQuery(id+"F5.opPattern","COPY",BODY,{"derivedFrom":makeQuery(id+"F4.opExtrude","SWEPT_BODY",BODY,{"disambiguationData":[OSD([sQuery(id+"F1.wireOp",EDGE,"E7"),sQuery(id+"F1.wireOp",EDGE,"E11"),sQuery(id+"F1.wireOp",EDGE,"E12")])]}),"instanceName":"49"});
            var Q99;
            Q99=makeQuery(id+"F5.opPattern","COPY",BODY,{"derivedFrom":makeQuery(id+"F4.opExtrude","SWEPT_BODY",BODY,{"disambiguationData":[OSD([sQuery(id+"F1.wireOp",EDGE,"E8"),sQuery(id+"F1.wireOp",EDGE,"E13"),sQuery(id+"F1.wireOp",EDGE,"E14")])]}),"instanceName":"49"});
            var Q100;
            Q100=makeQuery(id+"F5.opPattern","COPY",BODY,{"derivedFrom":makeQuery(id+"F4.opExtrude","SWEPT_BODY",BODY,{"disambiguationData":[OSD([sQuery(id+"F1.wireOp",EDGE,"E7"),sQuery(id+"F1.wireOp",EDGE,"E11"),sQuery(id+"F1.wireOp",EDGE,"E12")])]}),"instanceName":"50"});
            var Q101;
            Q101=makeQuery(id+"F5.opPattern","COPY",BODY,{"derivedFrom":makeQuery(id+"F4.opExtrude","SWEPT_BODY",BODY,{"disambiguationData":[OSD([sQuery(id+"F1.wireOp",EDGE,"E8"),sQuery(id+"F1.wireOp",EDGE,"E13"),sQuery(id+"F1.wireOp",EDGE,"E14")])]}),"instanceName":"50"});
            var Q102;
            Q102=makeQuery(id+"F5.opPattern","COPY",BODY,{"derivedFrom":makeQuery(id+"F4.opExtrude","SWEPT_BODY",BODY,{"disambiguationData":[OSD([sQuery(id+"F1.wireOp",EDGE,"E7"),sQuery(id+"F1.wireOp",EDGE,"E11"),sQuery(id+"F1.wireOp",EDGE,"E12")])]}),"instanceName":"51"});
            var Q103;
            Q103=makeQuery(id+"F5.opPattern","COPY",BODY,{"derivedFrom":makeQuery(id+"F4.opExtrude","SWEPT_BODY",BODY,{"disambiguationData":[OSD([sQuery(id+"F1.wireOp",EDGE,"E8"),sQuery(id+"F1.wireOp",EDGE,"E13"),sQuery(id+"F1.wireOp",EDGE,"E14")])]}),"instanceName":"51"});
            var Q104;
            Q104=makeQuery(id+"F5.opPattern","COPY",BODY,{"derivedFrom":makeQuery(id+"F4.opExtrude","SWEPT_BODY",BODY,{"disambiguationData":[OSD([sQuery(id+"F1.wireOp",EDGE,"E7"),sQuery(id+"F1.wireOp",EDGE,"E11"),sQuery(id+"F1.wireOp",EDGE,"E12")])]}),"instanceName":"52"});
            var Q105;
            Q105=makeQuery(id+"F5.opPattern","COPY",BODY,{"derivedFrom":makeQuery(id+"F4.opExtrude","SWEPT_BODY",BODY,{"disambiguationData":[OSD([sQuery(id+"F1.wireOp",EDGE,"E8"),sQuery(id+"F1.wireOp",EDGE,"E13"),sQuery(id+"F1.wireOp",EDGE,"E14")])]}),"instanceName":"52"});
            var Q106;
            Q106=makeQuery(id+"F5.opPattern","COPY",BODY,{"derivedFrom":makeQuery(id+"F4.opExtrude","SWEPT_BODY",BODY,{"disambiguationData":[OSD([sQuery(id+"F1.wireOp",EDGE,"E7"),sQuery(id+"F1.wireOp",EDGE,"E11"),sQuery(id+"F1.wireOp",EDGE,"E12")])]}),"instanceName":"53"});
            var Q107;
            Q107=makeQuery(id+"F5.opPattern","COPY",BODY,{"derivedFrom":makeQuery(id+"F4.opExtrude","SWEPT_BODY",BODY,{"disambiguationData":[OSD([sQuery(id+"F1.wireOp",EDGE,"E8"),sQuery(id+"F1.wireOp",EDGE,"E13"),sQuery(id+"F1.wireOp",EDGE,"E14")])]}),"instanceName":"53"});
            var Q108;
            Q108=makeQuery(id+"F5.opPattern","COPY",BODY,{"derivedFrom":makeQuery(id+"F4.opExtrude","SWEPT_BODY",BODY,{"disambiguationData":[OSD([sQuery(id+"F1.wireOp",EDGE,"E7"),sQuery(id+"F1.wireOp",EDGE,"E11"),sQuery(id+"F1.wireOp",EDGE,"E12")])]}),"instanceName":"54"});
            var Q109;
            Q109=makeQuery(id+"F5.opPattern","COPY",BODY,{"derivedFrom":makeQuery(id+"F4.opExtrude","SWEPT_BODY",BODY,{"disambiguationData":[OSD([sQuery(id+"F1.wireOp",EDGE,"E8"),sQuery(id+"F1.wireOp",EDGE,"E13"),sQuery(id+"F1.wireOp",EDGE,"E14")])]}),"instanceName":"54"});
            var Q110;
            Q110=makeQuery(id+"F5.opPattern","COPY",BODY,{"derivedFrom":makeQuery(id+"F4.opExtrude","SWEPT_BODY",BODY,{"disambiguationData":[OSD([sQuery(id+"F1.wireOp",EDGE,"E7"),sQuery(id+"F1.wireOp",EDGE,"E11"),sQuery(id+"F1.wireOp",EDGE,"E12")])]}),"instanceName":"55"});
            var Q111;
            Q111=makeQuery(id+"F5.opPattern","COPY",BODY,{"derivedFrom":makeQuery(id+"F4.opExtrude","SWEPT_BODY",BODY,{"disambiguationData":[OSD([sQuery(id+"F1.wireOp",EDGE,"E8"),sQuery(id+"F1.wireOp",EDGE,"E13"),sQuery(id+"F1.wireOp",EDGE,"E14")])]}),"instanceName":"55"});
            var Q112;
            Q112=makeQuery(id+"F5.opPattern","COPY",BODY,{"derivedFrom":makeQuery(id+"F4.opExtrude","SWEPT_BODY",BODY,{"disambiguationData":[OSD([sQuery(id+"F1.wireOp",EDGE,"E7"),sQuery(id+"F1.wireOp",EDGE,"E11"),sQuery(id+"F1.wireOp",EDGE,"E12")])]}),"instanceName":"56"});
            var Q113;
            Q113=makeQuery(id+"F5.opPattern","COPY",BODY,{"derivedFrom":makeQuery(id+"F4.opExtrude","SWEPT_BODY",BODY,{"disambiguationData":[OSD([sQuery(id+"F1.wireOp",EDGE,"E8"),sQuery(id+"F1.wireOp",EDGE,"E13"),sQuery(id+"F1.wireOp",EDGE,"E14")])]}),"instanceName":"56"});
            var Q114;
            Q114=makeQuery(id+"F5.opPattern","COPY",BODY,{"derivedFrom":makeQuery(id+"F4.opExtrude","SWEPT_BODY",BODY,{"disambiguationData":[OSD([sQuery(id+"F1.wireOp",EDGE,"E7"),sQuery(id+"F1.wireOp",EDGE,"E11"),sQuery(id+"F1.wireOp",EDGE,"E12")])]}),"instanceName":"57"});
            var Q115;
            Q115=makeQuery(id+"F5.opPattern","COPY",BODY,{"derivedFrom":makeQuery(id+"F4.opExtrude","SWEPT_BODY",BODY,{"disambiguationData":[OSD([sQuery(id+"F1.wireOp",EDGE,"E8"),sQuery(id+"F1.wireOp",EDGE,"E13"),sQuery(id+"F1.wireOp",EDGE,"E14")])]}),"instanceName":"57"});
            var Q116;
            Q116=makeQuery(id+"F5.opPattern","COPY",BODY,{"derivedFrom":makeQuery(id+"F4.opExtrude","SWEPT_BODY",BODY,{"disambiguationData":[OSD([sQuery(id+"F1.wireOp",EDGE,"E7"),sQuery(id+"F1.wireOp",EDGE,"E11"),sQuery(id+"F1.wireOp",EDGE,"E12")])]}),"instanceName":"58"});
            var Q117;
            Q117=makeQuery(id+"F5.opPattern","COPY",BODY,{"derivedFrom":makeQuery(id+"F4.opExtrude","SWEPT_BODY",BODY,{"disambiguationData":[OSD([sQuery(id+"F1.wireOp",EDGE,"E8"),sQuery(id+"F1.wireOp",EDGE,"E13"),sQuery(id+"F1.wireOp",EDGE,"E14")])]}),"instanceName":"58"});
            var Q118;
            Q118=makeQuery(id+"F5.opPattern","COPY",BODY,{"derivedFrom":makeQuery(id+"F4.opExtrude","SWEPT_BODY",BODY,{"disambiguationData":[OSD([sQuery(id+"F1.wireOp",EDGE,"E7"),sQuery(id+"F1.wireOp",EDGE,"E11"),sQuery(id+"F1.wireOp",EDGE,"E12")])]}),"instanceName":"59"});
            var Q119;
            Q119=makeQuery(id+"F5.opPattern","COPY",BODY,{"derivedFrom":makeQuery(id+"F4.opExtrude","SWEPT_BODY",BODY,{"disambiguationData":[OSD([sQuery(id+"F1.wireOp",EDGE,"E8"),sQuery(id+"F1.wireOp",EDGE,"E13"),sQuery(id+"F1.wireOp",EDGE,"E14")])]}),"instanceName":"59"});
            var Q120;
            Q120=makeQuery(id+"F5.opPattern","COPY",BODY,{"derivedFrom":makeQuery(id+"F4.opExtrude","SWEPT_BODY",BODY,{"disambiguationData":[OSD([sQuery(id+"F1.wireOp",EDGE,"E7"),sQuery(id+"F1.wireOp",EDGE,"E11"),sQuery(id+"F1.wireOp",EDGE,"E12")])]}),"instanceName":"60"});
            var Q121;
            Q121=makeQuery(id+"F5.opPattern","COPY",BODY,{"derivedFrom":makeQuery(id+"F4.opExtrude","SWEPT_BODY",BODY,{"disambiguationData":[OSD([sQuery(id+"F1.wireOp",EDGE,"E8"),sQuery(id+"F1.wireOp",EDGE,"E13"),sQuery(id+"F1.wireOp",EDGE,"E14")])]}),"instanceName":"60"});
            var Q122;
            Q122=makeQuery(id+"F5.opPattern","COPY",BODY,{"derivedFrom":makeQuery(id+"F4.opExtrude","SWEPT_BODY",BODY,{"disambiguationData":[OSD([sQuery(id+"F1.wireOp",EDGE,"E7"),sQuery(id+"F1.wireOp",EDGE,"E11"),sQuery(id+"F1.wireOp",EDGE,"E12")])]}),"instanceName":"61"});
            var Q123;
            Q123=makeQuery(id+"F5.opPattern","COPY",BODY,{"derivedFrom":makeQuery(id+"F4.opExtrude","SWEPT_BODY",BODY,{"disambiguationData":[OSD([sQuery(id+"F1.wireOp",EDGE,"E8"),sQuery(id+"F1.wireOp",EDGE,"E13"),sQuery(id+"F1.wireOp",EDGE,"E14")])]}),"instanceName":"61"});
            var Q124;
            Q124=makeQuery(id+"F5.opPattern","COPY",BODY,{"derivedFrom":makeQuery(id+"F4.opExtrude","SWEPT_BODY",BODY,{"disambiguationData":[OSD([sQuery(id+"F1.wireOp",EDGE,"E7"),sQuery(id+"F1.wireOp",EDGE,"E11"),sQuery(id+"F1.wireOp",EDGE,"E12")])]}),"instanceName":"62"});
            var Q125;
            Q125=makeQuery(id+"F5.opPattern","COPY",BODY,{"derivedFrom":makeQuery(id+"F4.opExtrude","SWEPT_BODY",BODY,{"disambiguationData":[OSD([sQuery(id+"F1.wireOp",EDGE,"E8"),sQuery(id+"F1.wireOp",EDGE,"E13"),sQuery(id+"F1.wireOp",EDGE,"E14")])]}),"instanceName":"62"});
            var Q126;
            Q126=makeQuery(id+"F5.opPattern","COPY",BODY,{"derivedFrom":makeQuery(id+"F4.opExtrude","SWEPT_BODY",BODY,{"disambiguationData":[OSD([sQuery(id+"F1.wireOp",EDGE,"E7"),sQuery(id+"F1.wireOp",EDGE,"E11"),sQuery(id+"F1.wireOp",EDGE,"E12")])]}),"instanceName":"63"});
            var Q127;
            Q127=makeQuery(id+"F5.opPattern","COPY",BODY,{"derivedFrom":makeQuery(id+"F4.opExtrude","SWEPT_BODY",BODY,{"disambiguationData":[OSD([sQuery(id+"F1.wireOp",EDGE,"E8"),sQuery(id+"F1.wireOp",EDGE,"E13"),sQuery(id+"F1.wireOp",EDGE,"E14")])]}),"instanceName":"63"});
            var Q128;
            Q128=makeQuery(id+"F5.opPattern","COPY",BODY,{"derivedFrom":makeQuery(id+"F4.opExtrude","SWEPT_BODY",BODY,{"disambiguationData":[OSD([sQuery(id+"F1.wireOp",EDGE,"E7"),sQuery(id+"F1.wireOp",EDGE,"E11"),sQuery(id+"F1.wireOp",EDGE,"E12")])]}),"instanceName":"64"});
            var Q129;
            Q129=makeQuery(id+"F5.opPattern","COPY",BODY,{"derivedFrom":makeQuery(id+"F4.opExtrude","SWEPT_BODY",BODY,{"disambiguationData":[OSD([sQuery(id+"F1.wireOp",EDGE,"E8"),sQuery(id+"F1.wireOp",EDGE,"E13"),sQuery(id+"F1.wireOp",EDGE,"E14")])]}),"instanceName":"64"});
            var Q130;
            Q130=makeQuery(id+"F5.opPattern","COPY",BODY,{"derivedFrom":makeQuery(id+"F4.opExtrude","SWEPT_BODY",BODY,{"disambiguationData":[OSD([sQuery(id+"F1.wireOp",EDGE,"E7"),sQuery(id+"F1.wireOp",EDGE,"E11"),sQuery(id+"F1.wireOp",EDGE,"E12")])]}),"instanceName":"65"});
            var Q131;
            Q131=makeQuery(id+"F5.opPattern","COPY",BODY,{"derivedFrom":makeQuery(id+"F4.opExtrude","SWEPT_BODY",BODY,{"disambiguationData":[OSD([sQuery(id+"F1.wireOp",EDGE,"E8"),sQuery(id+"F1.wireOp",EDGE,"E13"),sQuery(id+"F1.wireOp",EDGE,"E14")])]}),"instanceName":"65"});
            var Q132;
            Q132=makeQuery(id+"F5.opPattern","COPY",BODY,{"derivedFrom":makeQuery(id+"F4.opExtrude","SWEPT_BODY",BODY,{"disambiguationData":[OSD([sQuery(id+"F1.wireOp",EDGE,"E7"),sQuery(id+"F1.wireOp",EDGE,"E11"),sQuery(id+"F1.wireOp",EDGE,"E12")])]}),"instanceName":"66"});
            var Q133;
            Q133=makeQuery(id+"F5.opPattern","COPY",BODY,{"derivedFrom":makeQuery(id+"F4.opExtrude","SWEPT_BODY",BODY,{"disambiguationData":[OSD([sQuery(id+"F1.wireOp",EDGE,"E8"),sQuery(id+"F1.wireOp",EDGE,"E13"),sQuery(id+"F1.wireOp",EDGE,"E14")])]}),"instanceName":"66"});
            var Q134;
            Q134=makeQuery(id+"F5.opPattern","COPY",BODY,{"derivedFrom":makeQuery(id+"F4.opExtrude","SWEPT_BODY",BODY,{"disambiguationData":[OSD([sQuery(id+"F1.wireOp",EDGE,"E7"),sQuery(id+"F1.wireOp",EDGE,"E11"),sQuery(id+"F1.wireOp",EDGE,"E12")])]}),"instanceName":"67"});
            var Q135;
            Q135=makeQuery(id+"F5.opPattern","COPY",BODY,{"derivedFrom":makeQuery(id+"F4.opExtrude","SWEPT_BODY",BODY,{"disambiguationData":[OSD([sQuery(id+"F1.wireOp",EDGE,"E8"),sQuery(id+"F1.wireOp",EDGE,"E13"),sQuery(id+"F1.wireOp",EDGE,"E14")])]}),"instanceName":"67"});
            var Q136;
            Q136=makeQuery(id+"F5.opPattern","COPY",BODY,{"derivedFrom":makeQuery(id+"F4.opExtrude","SWEPT_BODY",BODY,{"disambiguationData":[OSD([sQuery(id+"F1.wireOp",EDGE,"E7"),sQuery(id+"F1.wireOp",EDGE,"E11"),sQuery(id+"F1.wireOp",EDGE,"E12")])]}),"instanceName":"68"});
            var Q137;
            Q137=makeQuery(id+"F5.opPattern","COPY",BODY,{"derivedFrom":makeQuery(id+"F4.opExtrude","SWEPT_BODY",BODY,{"disambiguationData":[OSD([sQuery(id+"F1.wireOp",EDGE,"E8"),sQuery(id+"F1.wireOp",EDGE,"E13"),sQuery(id+"F1.wireOp",EDGE,"E14")])]}),"instanceName":"68"});
            var Q138;
            Q138=makeQuery(id+"F5.opPattern","COPY",BODY,{"derivedFrom":makeQuery(id+"F4.opExtrude","SWEPT_BODY",BODY,{"disambiguationData":[OSD([sQuery(id+"F1.wireOp",EDGE,"E7"),sQuery(id+"F1.wireOp",EDGE,"E11"),sQuery(id+"F1.wireOp",EDGE,"E12")])]}),"instanceName":"69"});
            var Q139;
            Q139=makeQuery(id+"F5.opPattern","COPY",BODY,{"derivedFrom":makeQuery(id+"F4.opExtrude","SWEPT_BODY",BODY,{"disambiguationData":[OSD([sQuery(id+"F1.wireOp",EDGE,"E8"),sQuery(id+"F1.wireOp",EDGE,"E13"),sQuery(id+"F1.wireOp",EDGE,"E14")])]}),"instanceName":"69"});
            var Q140;
            Q140=makeQuery(id+"F2.opRevolve","SWEPT_BODY",BODY,{"disambiguationData":[OSD([sQuery(id+"F1.wireOp",EDGE,"E1"),sQuery(id+"F1.wireOp",EDGE,"E2"),sQuery(id+"F1.wireOp",EDGE,"E3"),sQuery(id+"F1.wireOp",EDGE,"E4"),sQuery(id+"F1.wireOp",EDGE,"E5"),sQuery(id+"F1.wireOp",EDGE,"E6"),sQuery(id+"F1.wireOp",EDGE,"E7"),sQuery(id+"F1.wireOp",EDGE,"E8"),sQuery(id+"F1.wireOp",EDGE,"E9"),sQuery(id+"F1.wireOp",EDGE,"E10")])]});
            booleanBodies(context, id + "F6", {"operationType" : BooleanOperationType.SUBTRACTION, "tools" : qUnion([Q0, Q1, Q2, Q3, Q4, Q5, Q6, Q7, Q8, Q9, Q10, Q11, Q12, Q13, Q14, Q15, Q16, Q17, Q18, Q19, Q20, Q21, Q22, Q23, Q24, Q25, Q26, Q27, Q28, Q29, Q30, Q31, Q32, Q33, Q34, Q35, Q36, Q37, Q38, Q39, Q40, Q41, Q42, Q43, Q44, Q45, Q46, Q47, Q48, Q49, Q50, Q51, Q52, Q53, Q54, Q55, Q56, Q57, Q58, Q59, Q60, Q61, Q62, Q63, Q64, Q65, Q66, Q67, Q68, Q69, Q70, Q71, Q72, Q73, Q74, Q75, Q76, Q77, Q78, Q79, Q80, Q81, Q82, Q83, Q84, Q85, Q86, Q87, Q88, Q89, Q90, Q91, Q92, Q93, Q94, Q95, Q96, Q97, Q98, Q99, Q100, Q101, Q102, Q103, Q104, Q105, Q106, Q107, Q108, Q109, Q110, Q111, Q112, Q113, Q114, Q115, Q116, Q117, Q118, Q119, Q120, Q121, Q122, Q123, Q124, Q125, Q126, Q127, Q128, Q129, Q130, Q131, Q132, Q133, Q134, Q135, Q136, Q137, Q138, Q139]), "targets" : qUnion([Q140])});
        }
        {
            var Q0;
            Q0=makeQuery(id+"F1.imprint","IMPRINT",FACE,{"disambiguationData":[TD([[makeQuery(id+"F1.imprint","IMPRINT",EDGE,{"derivedFrom":sQuery(id+"F1.wireOp",EDGE,"E8")}),1.0]])]});
            var Q1;
            Q1=makeQuery(id+"F1.imprint","IMPRINT",FACE,{"disambiguationData":[TD([[makeQuery(id+"F1.imprint","IMPRINT",EDGE,{"derivedFrom":sQuery(id+"F1.wireOp",EDGE,"E23")}),1.0]])]});
            var Q2;
            Q2=sQuery(id+"F0.wireOp",EDGE,"E0");
            revolve(context, id + "F7", {"entities" : qUnion([Q0, Q1]), "axis" : qUnion([Q2]), "revolveType" : RevolveType.FULL});
        }
        {
            var Q0;
            Q0=qCreatedBy(makeId("Right.planeOp"),FACE);
            cPlane(context, id + "F8", {"entities" : qUnion([Q0]), "cplaneType" : CPlaneType.OFFSET, "offset" : 57.35 * mm, "width" : 152.4 * mm, "height" : 152.4 * mm});
        }
        {
            var Q0;
            Q0=qCreatedBy(id+"F8.planeOp",FACE);
            var sketch = newSketch(context, id + "F9", { "sketchPlane" : qUnion([Q0])});
            skLineSegment(sketch, "E28", {"start": v(6.43, -3.35) * mm, "end": v(5.14, -0.23) * mm});
            skPoint(sketch, "E28.endSnap0", {"position": v(6.43, -0.23) * mm});
            skLineSegment(sketch, "E29", {"start": v(5.14, -0.23) * mm, "end": v(6.43, 2.89) * mm});
            skLineSegment(sketch, "E30", {"start": v(6.43, 2.89) * mm, "end": v(7.73, 2.89) * mm});
            skLineSegment(sketch, "E31", {"start": v(6.43, -3.35) * mm, "end": v(7.73, -3.35) * mm});
            skLineSegment(sketch, "E32", {"start": v(7.73, -3.35) * mm, "end": v(6.43, -0.23) * mm});
            skLineSegment(sketch, "E33", {"start": v(7.73, 2.89) * mm, "end": v(6.43, -0.23) * mm});
            skLineSegment(sketch, "E34", {"start": v(10.29, -3.35) * mm, "end": v(9, -0.23) * mm});
            skPoint(sketch, "E34.endSnap0", {"position": v(10.29, -0.23) * mm});
            skLineSegment(sketch, "E35", {"start": v(9, -0.23) * mm, "end": v(10.29, 2.89) * mm});
            skLineSegment(sketch, "E36", {"start": v(10.29, 2.89) * mm, "end": v(11.58, 2.89) * mm});
            skLineSegment(sketch, "E37", {"start": v(10.29, -3.35) * mm, "end": v(11.58, -3.35) * mm});
            skLineSegment(sketch, "E38", {"start": v(11.58, -3.35) * mm, "end": v(10.29, -0.23) * mm});
            skLineSegment(sketch, "E39", {"start": v(11.58, 2.89) * mm, "end": v(10.29, -0.23) * mm});
            skLineSegment(sketch, "E40", {"start": v(14.14, -3.35) * mm, "end": v(12.85, -0.23) * mm});
            skPoint(sketch, "E40.endSnap0", {"position": v(14.14, -0.23) * mm});
            skLineSegment(sketch, "E41", {"start": v(12.85, -0.23) * mm, "end": v(14.14, 2.89) * mm});
            skLineSegment(sketch, "E42", {"start": v(14.14, 2.89) * mm, "end": v(15.43, 2.89) * mm});
            skLineSegment(sketch, "E43", {"start": v(14.14, -3.35) * mm, "end": v(15.43, -3.35) * mm});
            skLineSegment(sketch, "E44", {"start": v(15.43, -3.35) * mm, "end": v(14.14, -0.23) * mm});
            skLineSegment(sketch, "E45", {"start": v(15.43, 2.89) * mm, "end": v(14.14, -0.23) * mm});
            skLineSegment(sketch, "E46", {"start": v(18, -3.35) * mm, "end": v(16.7, -0.23) * mm});
            skPoint(sketch, "E46.endSnap0", {"position": v(18, -0.23) * mm});
            skLineSegment(sketch, "E47", {"start": v(16.7, -0.23) * mm, "end": v(18, 2.89) * mm});
            skLineSegment(sketch, "E48", {"start": v(18, 2.89) * mm, "end": v(19.28, 2.89) * mm});
            skLineSegment(sketch, "E49", {"start": v(18, -3.35) * mm, "end": v(19.28, -3.35) * mm});
            skLineSegment(sketch, "E50", {"start": v(19.28, -3.35) * mm, "end": v(18, -0.23) * mm});
            skLineSegment(sketch, "E51", {"start": v(19.28, 2.89) * mm, "end": v(18, -0.23) * mm});
            skSolve(sketch);
        }
        {
            var Q0;
            Q0 = qSketchRegion(id + "F9", true);
            extrude(context, id + "F10", {"entities" : qUnion([Q0]), "depth" : 1.98 * mm});
        }
        {
            var Q0;
            Q0=makeQuery(id+"F10.opExtrude","SWEPT_BODY",BODY,{"disambiguationData":[OSD([sQuery(id+"F9.wireOp",EDGE,"E28"),sQuery(id+"F9.wireOp",EDGE,"E29"),sQuery(id+"F9.wireOp",EDGE,"E30"),sQuery(id+"F9.wireOp",EDGE,"E31"),sQuery(id+"F9.wireOp",EDGE,"E32"),sQuery(id+"F9.wireOp",EDGE,"E33")])]});
            var Q1;
            Q1=makeQuery(id+"F10.opExtrude","SWEPT_BODY",BODY,{"disambiguationData":[OSD([sQuery(id+"F9.wireOp",EDGE,"E34"),sQuery(id+"F9.wireOp",EDGE,"E35"),sQuery(id+"F9.wireOp",EDGE,"E36"),sQuery(id+"F9.wireOp",EDGE,"E37"),sQuery(id+"F9.wireOp",EDGE,"E38"),sQuery(id+"F9.wireOp",EDGE,"E39")])]});
            var Q2;
            Q2=makeQuery(id+"F10.opExtrude","SWEPT_BODY",BODY,{"disambiguationData":[OSD([sQuery(id+"F9.wireOp",EDGE,"E40"),sQuery(id+"F9.wireOp",EDGE,"E41"),sQuery(id+"F9.wireOp",EDGE,"E42"),sQuery(id+"F9.wireOp",EDGE,"E43"),sQuery(id+"F9.wireOp",EDGE,"E44"),sQuery(id+"F9.wireOp",EDGE,"E45")])]});
            var Q3;
            Q3=makeQuery(id+"F10.opExtrude","SWEPT_BODY",BODY,{"disambiguationData":[OSD([sQuery(id+"F9.wireOp",EDGE,"E46"),sQuery(id+"F9.wireOp",EDGE,"E47"),sQuery(id+"F9.wireOp",EDGE,"E48"),sQuery(id+"F9.wireOp",EDGE,"E49"),sQuery(id+"F9.wireOp",EDGE,"E50"),sQuery(id+"F9.wireOp",EDGE,"E51")])]});
            var Q4;
            Q4=makeQuery(id+"F2.opRevolve","SWEPT_EDGE",EDGE,{"disambiguationData":[OSD([sQuery(id+"F1.wireOp",EDGE,"E1"),sQuery(id+"F1.wireOp",EDGE,"E5")])]});
            circularPattern(context, id + "F11", {"entities" : qUnion([Q0, Q1, Q2, Q3]), "axis" : qUnion([Q4]), "angle" : 360 * degree, "instanceCount" : 60, "equalSpace" : true});
        }
        {
            var Q0;
            Q0=makeQuery(id+"F10.opExtrude","SWEPT_BODY",BODY,{"disambiguationData":[OSD([sQuery(id+"F9.wireOp",EDGE,"E28"),sQuery(id+"F9.wireOp",EDGE,"E29"),sQuery(id+"F9.wireOp",EDGE,"E30"),sQuery(id+"F9.wireOp",EDGE,"E31"),sQuery(id+"F9.wireOp",EDGE,"E32"),sQuery(id+"F9.wireOp",EDGE,"E33")])]});
            var Q1;
            Q1=makeQuery(id+"F10.opExtrude","SWEPT_BODY",BODY,{"disambiguationData":[OSD([sQuery(id+"F9.wireOp",EDGE,"E34"),sQuery(id+"F9.wireOp",EDGE,"E35"),sQuery(id+"F9.wireOp",EDGE,"E36"),sQuery(id+"F9.wireOp",EDGE,"E37"),sQuery(id+"F9.wireOp",EDGE,"E38"),sQuery(id+"F9.wireOp",EDGE,"E39")])]});
            var Q2;
            Q2=makeQuery(id+"F10.opExtrude","SWEPT_BODY",BODY,{"disambiguationData":[OSD([sQuery(id+"F9.wireOp",EDGE,"E40"),sQuery(id+"F9.wireOp",EDGE,"E41"),sQuery(id+"F9.wireOp",EDGE,"E42"),sQuery(id+"F9.wireOp",EDGE,"E43"),sQuery(id+"F9.wireOp",EDGE,"E44"),sQuery(id+"F9.wireOp",EDGE,"E45")])]});
            var Q3;
            Q3=makeQuery(id+"F10.opExtrude","SWEPT_BODY",BODY,{"disambiguationData":[OSD([sQuery(id+"F9.wireOp",EDGE,"E46"),sQuery(id+"F9.wireOp",EDGE,"E47"),sQuery(id+"F9.wireOp",EDGE,"E48"),sQuery(id+"F9.wireOp",EDGE,"E49"),sQuery(id+"F9.wireOp",EDGE,"E50"),sQuery(id+"F9.wireOp",EDGE,"E51")])]});
            var Q4;
            Q4=makeQuery(id+"F2.opRevolve","SWEPT_BODY",BODY,{"disambiguationData":[OSD([sQuery(id+"F1.wireOp",EDGE,"E1"),sQuery(id+"F1.wireOp",EDGE,"E2"),sQuery(id+"F1.wireOp",EDGE,"E3"),sQuery(id+"F1.wireOp",EDGE,"E4"),sQuery(id+"F1.wireOp",EDGE,"E5"),sQuery(id+"F1.wireOp",EDGE,"E6"),sQuery(id+"F1.wireOp",EDGE,"E7"),sQuery(id+"F1.wireOp",EDGE,"E9"),sQuery(id+"F1.wireOp",EDGE,"E10"),sQuery(id+"F1.wireOp",EDGE,"E15"),sQuery(id+"F1.wireOp",EDGE,"E16"),sQuery(id+"F1.wireOp",EDGE,"E17"),sQuery(id+"F1.wireOp",EDGE,"E18"),sQuery(id+"F1.wireOp",EDGE,"E19"),sQuery(id+"F1.wireOp",EDGE,"E20"),sQuery(id+"F1.wireOp",EDGE,"E22"),sQuery(id+"F1.wireOp",EDGE,"E24"),sQuery(id+"F1.wireOp",EDGE,"E25"),sQuery(id+"F1.wireOp",EDGE,"E26"),sQuery(id+"F1.wireOp",EDGE,"E27")])]});
            booleanBodies(context, id + "F12", {"operationType" : BooleanOperationType.SUBTRACTION, "tools" : qUnion([Q0, Q1, Q2, Q3]), "targets" : qUnion([Q4])});
        }
    });
